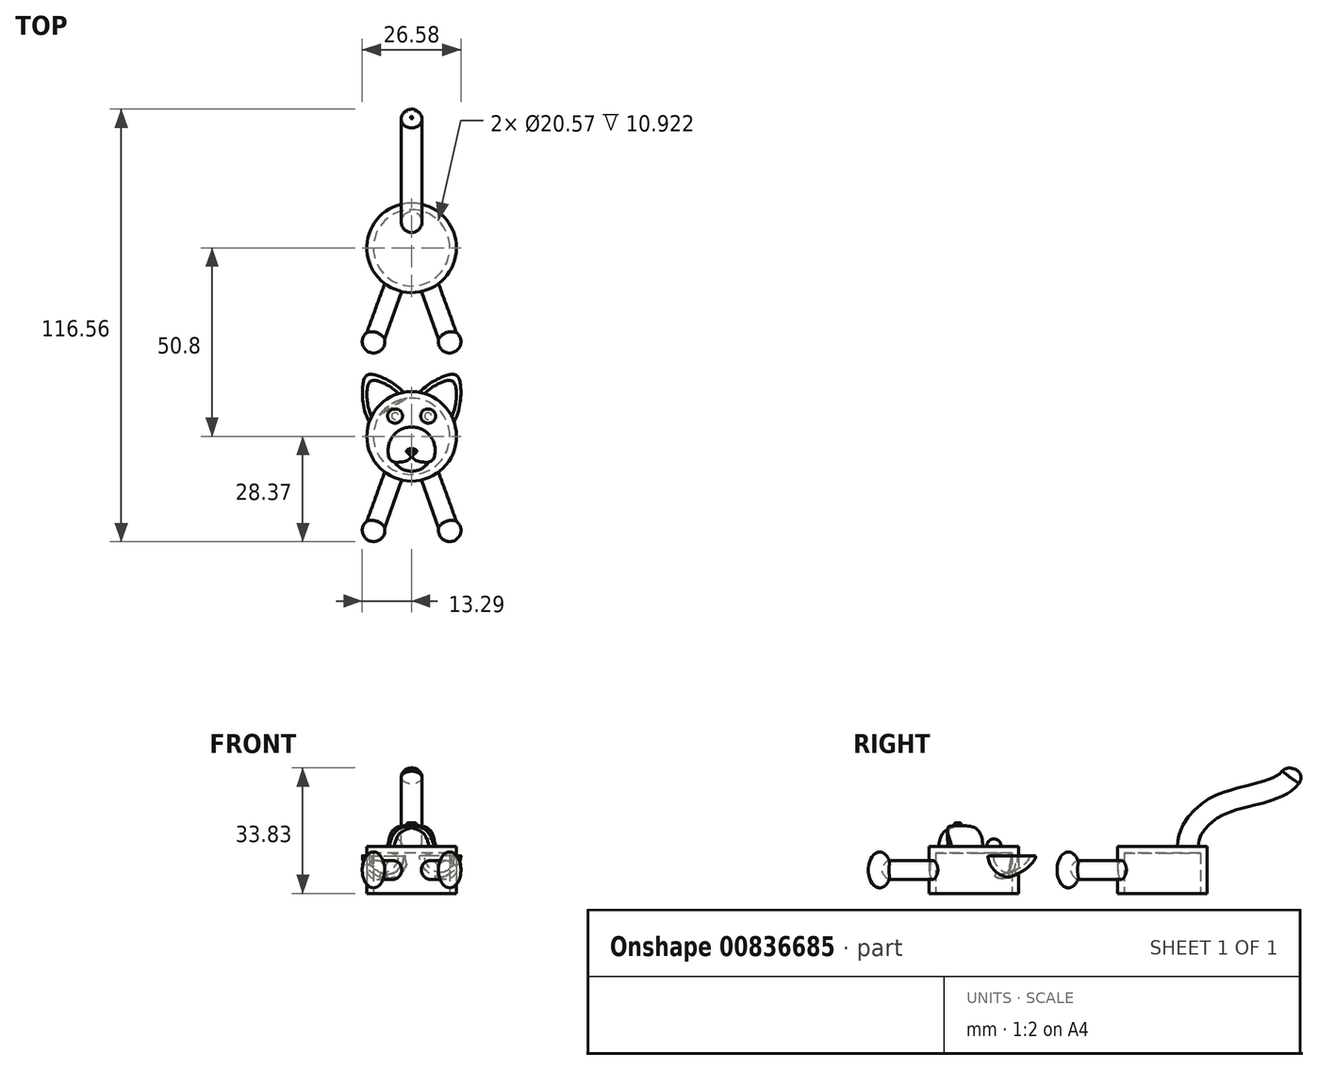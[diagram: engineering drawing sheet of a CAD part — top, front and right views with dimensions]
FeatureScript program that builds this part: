
annotation { "Feature Type Name" : "Feature", "Feature Type Description" : "" }
export const myFeature = defineFeature(function(context is Context, id is Id, definition is map)
    precondition{}
    {
        {
            var Q0;
            Q0=qCreatedBy(makeId("Top.planeOp"),FACE);
            var sketch = newSketch(context, id + "F0", { "sketchPlane" : qUnion([Q0])});
            skCircle(sketch, "E0", {"center": v(0, 0) * mm, "radius": 12.07 * mm});
            skLineSegment(sketch, "E1", {"start": v(-13.52, -7.92) * mm, "end": v(3.44, -14.1) * mm, "construction": true});
            skLineSegment(sketch, "E2", {"start": v(0, 0) * mm, "end": v(0, -12.07) * mm, "construction": true});
            skLineSegment(sketch, "E3", {"start": v(4.26, -12.07) * mm, "end": v(-6.84, -12.07) * mm, "construction": true});
            skSolve(sketch);
        }
        {
            var Q0;
            Q0=makeQuery(id+"F0.imprint","IMPRINT",FACE,{"disambiguationData":[TD([[makeQuery(id+"F0.imprint","IMPRINT",EDGE,{"derivedFrom":sQuery(id+"F0.wireOp",EDGE,"E0")}),1.0]])]});
            var Q1;
            Q1=makeQuery(id+"F0.imprint","IMPRINT",FACE,{"disambiguationData":[TD([[makeQuery(id+"F0.imprint","IMPRINT",EDGE,{"derivedFrom":sQuery(id+"F0.wireOp",EDGE,"9b25e7be-1691-43c6-9166-aadb0c126e80")}),1.0]])]});
            var Q2;
            Q2=sQuery(id+"F0.wireOp",EDGE,"E0");
            extrude(context, id + "F1", {"entities" : qUnion([Q0, Q1]), "surfaceEntities" : qUnion([Q2]), "depth" : 12.7 * mm});
        }
        {
            var Q0;
            Q0=makeQuery(id+"F1.opExtrude","CAP_FACE",FACE,{"disambiguationData":[OSD([sQuery(id+"F0.wireOp",EDGE,"E0")])],"isStart":true});
            var Q1;
            Q1=makeQuery(id+"F1.opExtrude","CAP_FACE",FACE,{"disambiguationData":[OSD([sQuery(id+"F0.wireOp",EDGE,"9b25e7be-1691-43c6-9166-aadb0c126e80")])],"isStart":true});
            shell(context, id + "F2", {"entities" : qUnion([Q0, Q1]), "thickness" : 1.78 * mm});
        }
        {
            var Q0;
            Q0=sQuery(id+"F0.wireOp",EDGE,"E1");
            cPlane(context, id + "F3", {"entities" : qUnion([Q0]), "cplaneType" : CPlaneType.LINE_ANGLE, "offset" : 152.4 * mm, "angle" : 180 * degree, "width" : 152.4 * mm, "height" : 152.4 * mm});
        }
        {
            var Q0;
            Q0=qCreatedBy(id+"F3.planeOp",FACE);
            var sketch = newSketch(context, id + "F4", { "sketchPlane" : qUnion([Q0])});
            skCircle(sketch, "E4", {"center": v(1.08, 6.35) * mm, "radius": 2.54 * mm});
            skLineSegment(sketch, "E5", {"start": v(1.27, 0) * mm, "end": v(0.89, 12.7) * mm});
            skSolve(sketch);
        }
        {
            var Q0;
            Q0=makeQuery(id+"F1.opExtrude","SWEPT_BODY",BODY,{"disambiguationData":[OSD([sQuery(id+"F0.wireOp",EDGE,"E0")])]});
            transform(context, id + "F5", {"entities" : qUnion([Q0]), "transformType" : TransformType.TRANSLATION_3D, "dx" : 0 * mm, "dy" : 50.8 * mm, "dz" : 0 * mm, "makeCopy" : true});
        }
        {
            var Q0;
            Q0=qCreatedBy(makeId("Right.planeOp"),FACE);
            var sketch = newSketch(context, id + "F6", { "sketchPlane" : qUnion([Q0])});
            skPoint(sketch, "E6", {"position": v(-13.02, 12.7) * mm});
            skLineSegment(sketch, "E7", {"start": v(-13.02, 12.7) * mm, "end": v(7.91, 12.7) * mm, "construction": true});
            skFitSpline(sketch, "E8.0.MirrorCS", {"points": [v(2.53, 12.7) * mm, v(-3.82, 18.32) * mm], "startDerivative": vector(-1.37, 16.87) * mm, "endDerivative": vector(-11.47, 0.53) * mm});
            skLineSegment(sketch, "E9.0.MirrorCS", {"start": v(-3.82, 12.7) * mm, "end": v(2.53, 12.7) * mm});
            skLineSegment(sketch, "E10", {"start": v(-3.82, 12.7) * mm, "end": v(-3.82, 18.32) * mm});
            skLineSegment(sketch, "E11", {"start": v(-9.4, 12.7) * mm, "end": v(-4.2, 12.7) * mm});
            skLineSegment(sketch, "E12", {"start": v(-4.2, 12.7) * mm, "end": v(-4.2, 17.91) * mm});
            skFitSpline(sketch, "E13", {"points": [v(-9.4, 12.7) * mm, v(-8, 16.51) * mm, v(-4.2, 17.91) * mm], "startDerivative": vector(0.83, 9.2) * mm, "endDerivative": vector(8.62, 0.45) * mm});
            skSolve(sketch);
        }
        {
            var Q0;
            Q0=makeQuery(id+"F6.imprint","IMPRINT",FACE,{"disambiguationData":[TD([[makeQuery(id+"F6.imprint","IMPRINT",EDGE,{"derivedFrom":sQuery(id+"F6.wireOp",EDGE,"E8.0.MirrorCS")}),1.0]])]});
            var Q1;
            Q1=sQuery(id+"F6.wireOp",EDGE,"E10");
            revolve(context, id + "F7", {"operationType" : NewBodyOperationType.ADD, "entities" : qUnion([Q0]), "axis" : qUnion([Q1]), "revolveType" : RevolveType.FULL});
        }
        {
            var Q0;
            Q0=makeQuery(id+"F1.opExtrude","CAP_FACE",FACE,{"disambiguationData":[OSD([sQuery(id+"F0.wireOp",EDGE,"E0")])],"isStart":false});
            var sketch = newSketch(context, id + "F8", { "sketchPlane" : qUnion([Q0])});
            skCircle(sketch, "E14", {"center": v(4.58, 5.47) * mm, "radius": 1.9 * mm});
            skLineSegment(sketch, "E15", {"start": v(4.36, 3.58) * mm, "end": v(4.58, 7.38) * mm});
            skSolve(sketch);
        }
        {
            var Q0;
            {var subQ0=sQuery(id+"F8.wireOp",EDGE,"E15");Q0=makeQuery(id+"F8.imprint","IMPRINT",FACE,{"disambiguationData":[TD([[makeQuery(id+"F8.imprint","IMPRINT",EDGE,{"derivedFrom":subQ0}),-1.0]])]});}
            var Q1;
            Q1=sQuery(id+"F8.wireOp",EDGE,"E15");
            revolve(context, id + "F9", {"entities" : qUnion([Q0]), "axis" : qUnion([Q1]), "revolveType" : RevolveType.FULL});
        }
        {
            var Q0;
            Q0=makeQuery(id+"F9.opRevolve","SWEPT_BODY",BODY,{"disambiguationData":[OSD([sQuery(id+"F8.wireOp",EDGE,"E14"),sQuery(id+"F8.wireOp",EDGE,"E15")])]});
            var Q1;
            Q1=qCreatedBy(makeId("Right.planeOp"),FACE);
            mirror(context, id + "F10", {"operationType" : NewBodyOperationType.ADD, "entities" : qUnion([Q0]), "mirrorPlane" : qUnion([Q1])});
        }
        {
            var Q0;
            Q0=qCreatedBy(makeId("Top.planeOp"),FACE);
            cPlane(context, id + "F11", {"entities" : qUnion([Q0]), "cplaneType" : CPlaneType.OFFSET, "offset" : 19.05 * mm, "width" : 152.4 * mm, "height" : 152.4 * mm});
        }
        {
            var Q0;
            Q0=qCreatedBy(id+"F11.planeOp",FACE);
            var sketch = newSketch(context, id + "F12", { "sketchPlane" : qUnion([Q0])});
            skFitSpline(sketch, "E16", {"points": [v(-5.97, -5.99) * mm, v(-3.36, -6.97) * mm, v(0, -5.31) * mm], "startDerivative": vector(6.87, -7.35) * mm, "endDerivative": vector(4.34, 7.95) * mm});
            skFitSpline(sketch, "E17", {"points": [v(-5.97, -11.07) * mm, v(-3.36, -12.05) * mm, v(0, -10.4) * mm], "startDerivative": vector(6.87, -7.35) * mm, "endDerivative": vector(4.34, 7.95) * mm});
            skLineSegment(sketch, "E18", {"start": v(-5.97, -5.99) * mm, "end": v(-5.97, -11.07) * mm});
            skLineSegment(sketch, "E19", {"start": v(-4.9, -7.12) * mm, "end": v(-4.9, -12.2) * mm, "construction": true});
            skLineSegment(sketch, "E20", {"start": v(-3.36, -6.97) * mm, "end": v(-3.36, -12.05) * mm, "construction": true});
            skLineSegment(sketch, "E21", {"start": v(-0.78, -6.73) * mm, "end": v(-0.78, -11.81) * mm, "construction": true});
            skLineSegment(sketch, "E22", {"start": v(0, -5.31) * mm, "end": v(0, -10.4) * mm, "construction": true});
            skFitSpline(sketch, "E23.0.MirrorCS", {"points": [v(5.97, -5.99) * mm, v(3.36, -6.97) * mm, v(0, -5.31) * mm], "startDerivative": vector(-6.87, -7.35) * mm, "endDerivative": vector(-4.34, 7.95) * mm});
            skLineSegment(sketch, "E24.0.MirrorCS", {"start": v(5.97, -5.99) * mm, "end": v(5.97, -11.07) * mm});
            skFitSpline(sketch, "E25.0.MirrorCS", {"points": [v(5.97, -11.07) * mm, v(3.36, -12.05) * mm, v(0, -10.4) * mm], "startDerivative": vector(-6.87, -7.35) * mm, "endDerivative": vector(-4.34, 7.95) * mm});
            skFitSpline(sketch, "E26", {"points": [v(0, -5.31) * mm, v(-1.08, -4.5) * mm, v(-1.28, -3.73) * mm, v(0, -3.3) * mm], "startDerivative": vector(-1.6, 0.42) * mm, "endDerivative": vector(3.1, -0.16) * mm});
            skFitSpline(sketch, "E27.0.MirrorCS", {"points": [v(0, -5.31) * mm, v(1.08, -4.5) * mm, v(1.28, -3.73) * mm, v(0, -3.3) * mm], "startDerivative": vector(1.6, 0.42) * mm, "endDerivative": vector(-3.1, -0.16) * mm});
            skSolve(sketch);
        }
        {
            var Q0;
            Q0=makeQuery(id+"F12.imprint","IMPRINT",FACE,{"disambiguationData":[TD([[makeQuery(id+"F12.imprint","IMPRINT",EDGE,{"derivedFrom":sQuery(id+"F12.wireOp",EDGE,"E16")}),-1.0]])]});
            var Q1;
            Q1=makeQuery(id+"F1.opExtrude","CAP_FACE",FACE,{"disambiguationData":[OSD([sQuery(id+"F0.wireOp",EDGE,"E0")])],"isStart":false});
            extrude(context, id + "F13", {"entities" : qUnion([Q0]), "operationType" : NewBodyOperationType.REMOVE, "endBound" : BoundingType.UP_TO_SURFACE, "oppositeDirection" : true, "endBoundEntityFace" : qUnion([Q1]), "depth" : 25.4 * mm});
        }
        {
            var Q0;
            Q0=makeQuery(id+"F6.imprint","IMPRINT",FACE,{"disambiguationData":[TD([[makeQuery(id+"F6.imprint","IMPRINT",EDGE,{"derivedFrom":sQuery(id+"F6.wireOp",EDGE,"E11")}),1.0]])]});
            var Q1;
            Q1=sQuery(id+"F6.wireOp",EDGE,"E10");
            revolve(context, id + "F14", {"operationType" : NewBodyOperationType.ADD, "entities" : qUnion([Q0]), "axis" : qUnion([Q1]), "revolveType" : RevolveType.FULL});
        }
        {
            var Q0;
            Q0=makeQuery(id+"F12.imprint","IMPRINT",FACE,{"disambiguationData":[TD([[makeQuery(id+"F12.imprint","IMPRINT",EDGE,{"derivedFrom":sQuery(id+"F12.wireOp",EDGE,"E26")}),-1.0]])]});
            extrude(context, id + "F15", {"entities" : qUnion([Q0]), "operationType" : NewBodyOperationType.ADD, "oppositeDirection" : true, "depth" : 1.27 * mm});
        }
        {
            var Q0;
            Q0=qCreatedBy(makeId("Top.planeOp"),FACE);
            cPlane(context, id + "F16", {"entities" : qUnion([Q0]), "cplaneType" : CPlaneType.OFFSET, "offset" : 10.16 * mm, "width" : 152.4 * mm, "height" : 152.4 * mm});
        }
        {
            var Q0;
            Q0=qCreatedBy(id+"F16.planeOp",FACE);
            var sketch = newSketch(context, id + "F17", { "sketchPlane" : qUnion([Q0])});
            skFitSpline(sketch, "E28", {"points": [v(-12.05, 16.53) * mm, v(-13.13, 14) * mm, v(-11.42, 3.88) * mm], "startDerivative": vector(-6.43, -6.46) * mm, "endDerivative": vector(9.41, -17.97) * mm});
            skLineSegment(sketch, "E29", {"start": v(-12.05, 16.53) * mm, "end": v(-6.84, 8.2) * mm});
            skLineSegment(sketch, "E30", {"start": v(-11.42, 3.88) * mm, "end": v(-6.84, 8.2) * mm});
            skFitSpline(sketch, "E31", {"points": [v(-11.03, 14.9) * mm, v(-11.99, 12.7) * mm, v(-10.02, 3.47) * mm], "startDerivative": vector(-6.43, -6.46) * mm, "endDerivative": vector(9.41, -17.97) * mm});
            skLineSegment(sketch, "E32", {"start": v(-11.03, 14.9) * mm, "end": v(-6.05, 6.98) * mm});
            skLineSegment(sketch, "E33", {"start": v(-10.02, 3.47) * mm, "end": v(-6.05, 6.98) * mm});
            skSolve(sketch);
        }
        {
            var Q0;
            Q0=makeQuery(id+"F17.imprint","IMPRINT",FACE,{"disambiguationData":[TD([[makeQuery(id+"F17.imprint","IMPRINT",EDGE,{"derivedFrom":sQuery(id+"F17.wireOp",EDGE,"E28")}),1.0]])]});
            var Q1;
            Q1=sQuery(id+"F17.wireOp",EDGE,"E29");
            revolve(context, id + "F18", {"operationType" : NewBodyOperationType.ADD, "entities" : qUnion([Q0]), "axis" : qUnion([Q1]), "revolveType" : RevolveType.ONE_DIRECTION, "angle" : 180 * degree});
        }
        {
            var Q0;
            {var subQ0=sQuery(id+"F17.wireOp",EDGE,"E28");Q0=makeQuery(id+"F18.boolean.opBoolean","SPLIT",FACE,{"disambiguationData":[TD([makeQuery(id+"F1.opExtrude","SWEPT_FACE",FACE,{"disambiguationData":[OSD([sQuery(id+"F0.wireOp",EDGE,"E0")])]})])],"derivedFrom":makeQuery(id+"F18.opRevolve","CAP_FACE",FACE,{"disambiguationData":[OSD([subQ0,sQuery(id+"F17.wireOp",EDGE,"E29"),sQuery(id+"F17.wireOp",EDGE,"E30")])],"isStart":true})});}
            var Q1;
            {var subQ0=sQuery(id+"F17.wireOp",EDGE,"E28");Q1=makeQuery(id+"F18.boolean.opBoolean","SPLIT",FACE,{"disambiguationData":[TD([makeQuery(id+"F1.opExtrude","SWEPT_FACE",FACE,{"disambiguationData":[OSD([sQuery(id+"F0.wireOp",EDGE,"E0")])]})])],"derivedFrom":makeQuery(id+"F18.opRevolve","SWEPT_FACE",FACE,{"disambiguationData":[OSD([subQ0])]})});}
            var Q2;
            {var subQ0=sQuery(id+"F17.wireOp",EDGE,"E31");Q2=makeQuery(id+"F18.boolean.opBoolean","SPLIT",FACE,{"disambiguationData":[TD([makeQuery(id+"F1.opExtrude","SWEPT_FACE",FACE,{"disambiguationData":[OSD([sQuery(id+"F0.wireOp",EDGE,"E0")])]})])],"derivedFrom":makeQuery(id+"F18.opRevolve","SWEPT_FACE",FACE,{"disambiguationData":[OSD([subQ0])]})});}
            var Q3;
            Q3=qCreatedBy(makeId("Right.planeOp"),FACE);
            mirror(context, id + "F19", {"faces" : qUnion([Q0, Q1, Q2]), "mirrorPlane" : qUnion([Q3]), "patternType" : MirrorType.FACE});
        }
        {
            var Q0;
            Q0=makeQuery(id+"F15.opExtrude","CAP_EDGE",EDGE,{"disambiguationData":[OSD([sQuery(id+"F12.wireOp",EDGE,"E26")])],"isStart":true});
            var Q1;
            Q1=makeQuery(id+"F15.opExtrude","CAP_EDGE",EDGE,{"disambiguationData":[OSD([sQuery(id+"F12.wireOp",EDGE,"E27.0.MirrorCS")])],"isStart":true});
            var Q2;
            Q2=makeQuery(id+"F15.opExtrude","SWEPT_EDGE",EDGE,{"disambiguationData":[OSD([sQuery(id+"F12.wireOp",EDGE,"E16"),sQuery(id+"F12.wireOp",EDGE,"E23.0.MirrorCS"),sQuery(id+"F12.wireOp",EDGE,"E26"),sQuery(id+"F12.wireOp",EDGE,"E27.0.MirrorCS")])]});
            fillet(context, id + "F20", {"entities" : qUnion([Q0, Q1, Q2]), "radius" : 0.5 * mm, "allowEdgeOverflow" : false});
        }
        {
            var Q0;
            Q0=qCreatedBy(id+"F3.planeOp",FACE);
            var sketch = newSketch(context, id + "F21", { "sketchPlane" : qUnion([Q0])});
            skCircle(sketch, "E34", {"center": v(-0.97, 6.35) * mm, "radius": 2.54 * mm});
            skLineSegment(sketch, "E35", {"start": v(-0.97, 8.89) * mm, "end": v(-0.97, 3.8) * mm, "construction": true});
            skPoint(sketch, "E36", {"position": v(-0.97, 3.8) * mm});
            skPoint(sketch, "E37", {"position": v(-0.97, 8.89) * mm});
            skLineSegment(sketch, "E38", {"start": v(-0.97, 0) * mm, "end": v(-0.97, 12.7) * mm, "construction": true});
            skSolve(sketch);
        }
        {
            var Q0;
            Q0=makeQuery(id+"F21.imprint","IMPRINT",FACE,{"disambiguationData":[TD([[makeQuery(id+"F21.imprint","IMPRINT",EDGE,{"derivedFrom":sQuery(id+"F21.wireOp",EDGE,"E34")}),1.0]])]});
            extrude(context, id + "F22", {"entities" : qUnion([Q0]), "depth" : 15.24 * mm, "offsetDistance" : 25.4 * mm, "hasSecondDirection" : true, "secondDirectionBound" : SecondDirectionBoundingType.UP_TO_NEXT, "secondDirectionOppositeDirection" : true, "secondDirectionDepth" : 25.4 * mm});
        }
        {
            var Q0;
            Q0=makeQuery(id+"F22.opExtrude","CAP_FACE",FACE,{"disambiguationData":[OSD([sQuery(id+"F21.wireOp",EDGE,"E34")])],"isStart":false});
            var sketch = newSketch(context, id + "F23", { "sketchPlane" : qUnion([Q0])});
            skPoint(sketch, "E39", {"position": v(-0.97, 6.35) * mm});
            skSolve(sketch);
        }
        {
            var Q0;
            Q0=sQuery(id+"F21.wireOp",VERTEX,"E36");
            var Q1;
            Q1=sQuery(id+"F21.wireOp",VERTEX,"E37");
            var Q2;
            Q2=sQuery(id+"F23.wireOp",VERTEX,"E39");
            cPlane(context, id + "F24", {"entities" : qUnion([Q0, Q1, Q2]), "cplaneType" : CPlaneType.THREE_POINT, "offset" : 152.4 * mm, "width" : 152.4 * mm, "height" : 152.4 * mm});
        }
        {
            var Q0;
            Q0=qCreatedBy(id+"F24.planeOp",FACE);
            var sketch = newSketch(context, id + "F25", { "sketchPlane" : qUnion([Q0])});
            skEllipse(sketch, "E40", {"center": v(27.3, 6.35) * mm, "majorRadius": 4.83 * mm, "minorRadius": 3.05 * mm, "majorAxis": v(0, 1)});
            skLineSegment(sketch, "E41.rect.bottom", {"start": v(30.35, 11.18) * mm, "end": v(24.26, 11.18) * mm, "construction": true});
            skLineSegment(sketch, "E41.rect.top", {"start": v(30.35, 1.52) * mm, "end": v(24.26, 1.52) * mm, "construction": true});
            skLineSegment(sketch, "E41.rect.left", {"start": v(30.35, 11.18) * mm, "end": v(30.35, 1.52) * mm, "construction": true});
            skLineSegment(sketch, "E41.rect.right", {"start": v(24.26, 11.18) * mm, "end": v(24.26, 1.52) * mm, "construction": true});
            skPoint(sketch, "E42", {"position": v(27.3, 11.18) * mm});
            skPoint(sketch, "E43", {"position": v(30.35, 6.35) * mm});
            skLineSegment(sketch, "E44", {"start": v(27.3, 11.18) * mm, "end": v(27.3, 1.52) * mm});
            skSolve(sketch);
        }
        {
            var Q0;
            {var subQ0=sQuery(id+"F25.wireOp",EDGE,"E44");Q0=makeQuery(id+"F25.imprint","IMPRINT",FACE,{"disambiguationData":[TD([[makeQuery(id+"F25.imprint","IMPRINT",EDGE,{"derivedFrom":subQ0}),1.0]])]});}
            var Q1;
            Q1=sQuery(id+"F25.wireOp",EDGE,"E40");
            var Q2;
            Q2=sQuery(id+"F25.wireOp",EDGE,"E44");
            revolve(context, id + "F26", {"operationType" : NewBodyOperationType.ADD, "surfaceOperationType" : NewSurfaceOperationType.NEW, "entities" : qUnion([Q0]), "surfaceEntities" : qUnion([Q1]), "axis" : qUnion([Q2]), "revolveType" : RevolveType.FULL});
        }
        {
            var Q0;
            Q0=qCreatedBy(makeId("Top.planeOp"),FACE);
            var sketch = newSketch(context, id + "F27", { "sketchPlane" : qUnion([Q0])});
            skLineSegment(sketch, "E45", {"start": v(-5.04, -11) * mm, "end": v(-5.04, 39.84) * mm});
            skSolve(sketch);
        }
        {
            var Q0;
            Q0=makeQuery(id+"F22.opExtrude","SWEPT_BODY",BODY,{"disambiguationData":[OSD([sQuery(id+"F21.wireOp",EDGE,"E34")])]});
            var Q1;
            Q1=sQuery(id+"F27.wireOp",EDGE,"E45");
            transform(context, id + "F28", {"entities" : qUnion([Q0]), "transformType" : TransformType.TRANSLATION_ENTITY, "oppositeDirectionEntity" : false, "transformLine" : qUnion([Q1]), "makeCopy" : true});
        }
        {
            var Q0;
            Q0=makeQuery(id+"F22.opExtrude","SWEPT_BODY",BODY,{"disambiguationData":[OSD([sQuery(id+"F21.wireOp",EDGE,"E34")])]});
            var Q1;
            Q1=makeQuery(id+"F28.opPattern","COPY",BODY,{"derivedFrom":makeQuery(id+"F22.opExtrude","SWEPT_BODY",BODY,{"disambiguationData":[OSD([sQuery(id+"F21.wireOp",EDGE,"E34")])]}),"instanceName":"1"});
            var Q2;
            Q2=qCreatedBy(makeId("Right.planeOp"),FACE);
            mirror(context, id + "F29", {"operationType" : NewBodyOperationType.ADD, "entities" : qUnion([Q0, Q1]), "mirrorPlane" : qUnion([Q2])});
        }
        {
            var Q0;
            Q0=makeQuery(id+"F5.opPattern","COPY",FACE,{"derivedFrom":makeQuery(id+"F1.opExtrude","CAP_FACE",FACE,{"disambiguationData":[OSD([sQuery(id+"F0.wireOp",EDGE,"E0")])],"isStart":false}),"instanceName":"1"});
            var sketch = newSketch(context, id + "F30", { "sketchPlane" : qUnion([Q0])});
            skCircle(sketch, "E46", {"center": v(0, 57.74) * mm, "radius": 2.8 * mm});
            skSolve(sketch);
        }
        {
            var Q0;
            Q0=qCreatedBy(makeId("Right.planeOp"),FACE);
            var sketch = newSketch(context, id + "F31", { "sketchPlane" : qUnion([Q0])});
            skFitSpline(sketch, "E47", {"points": [v(57.74, 12.7) * mm, v(64.32, 22.77) * mm, v(75.24, 26.56) * mm, v(86.5, 33.55) * mm], "startDerivative": vector(0, 40.84) * mm, "endDerivative": vector(8.59, 37.02) * mm});
            skSolve(sketch);
        }
        {
            var Q0;
            Q0=makeQuery(id+"F30.imprint","IMPRINT",FACE,{"disambiguationData":[TD([[makeQuery(id+"F30.imprint","IMPRINT",EDGE,{"derivedFrom":sQuery(id+"F30.wireOp",EDGE,"E46")}),1.0]])]});
            var Q1;
            Q1=sQuery(id+"F31.wireOp",EDGE,"E47");
            sweep(context, id + "F32", {"operationType" : NewBodyOperationType.ADD, "profiles" : qUnion([Q0]), "path" : qUnion([Q1])});
        }
        {
            var Q0;
            Q0=makeQuery(id+"F32.opSweep","CAP_EDGE",EDGE,{"disambiguationData":[OSD([sQuery(id+"F30.wireOp",EDGE,"E46"),sQuery(id+"F31.wireOp",VERTEX,"E47.end")])],"isStart":false});
            fillet(context, id + "F33", {"entities" : qUnion([Q0]), "radius" : 2.5 * mm, "tangentPropagation" : true, "allowEdgeOverflow" : false});
        }
    });
